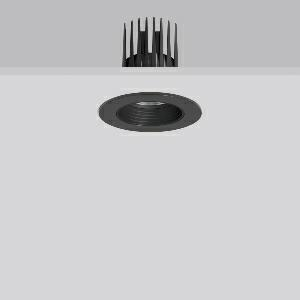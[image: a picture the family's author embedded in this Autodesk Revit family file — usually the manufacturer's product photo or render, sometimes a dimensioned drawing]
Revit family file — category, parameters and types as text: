
# Revit family: heledon_mini_e_901743_003_2_76_d9f7
name_source: partatom
category: Lighting Fixtures
units: mm (PartAtom-declared; Revit-internal decimal feet)

## family parameters
Cut with Voids When Loaded = No
Host = Face
Light Source = No
Part Type = Normal
Room Calculation Point = No
Round Connector Dimension = Use Diameter
Shared = No

## types (1)
- HELEDON mini E (1 x LED Modul 927, 2100 lm, 2700)
    Apparent Load = 20 VA
    Approval mark = CE
    CIE Flux Codes = 99 100 100 100 100
    Color Rendering = 92
    Color Temperature = 2700
    Default Elevation = 1800 mm
    Description = Series: HELEDON mini
Round recessed downlight. Housing: die-cast aluminium, powder-coated. Black plastic ring and recessed LED to prevent glare from the side. Optical assembly with lens made of plastic (polycarbonate) for the best homogeneous light distribution - can be changed without tools. Best colour rendering index Ra>90. Suitable for Recessed ceiling mounting. Installation without tools thanks to spring fastening system. Including separate LED converter with connecting cable 600 mm.High quality converter without flickering and stroboscopic effect. Through-wiring box (5 pole) available as accessory. The following accessories can be mounted without use of tools: interchangeable lenses, decorative glasses, honeycomb louvre, clear and frosted diffusers, white interchangeable plastic ring. 
Colour: deep black, matt (RAL 9005)
Diameter: 124 mm
Height: 3 mm
Cut-out diameter: 114 mm
Recess height: 170 mm
Luminaire: recess height: 120 mm
Lamp: LED
Socket: without socket
Colour temperature: 2700K
Colour rendering index (CRI): 92
System power: 20 W
Rated luminous flux: 2100 lm
Luminous efficiency: 105 lm/W
Control gear: Converter, dimmable, DALI
Protection class: II
Type of protection: IP 20
    Height = 0 mm  [stored 0 ft]
    Lamp = 1 x LED Modul 927
    Lamp Light Flux = 2100 lm
    Lamp count = 1
    Length = 124 mm  [stored 0.406824 ft]
    Lifetime = 50000 h
    Luminous efficacy = 105 lm/W
    Manufacturer = RZB
    ModVariant = No
    Model = 901743.003.2.76
    Mounting Place = Ceiling
    Mounting Type = Recessed
    Number of Poles = 1
    OnlyDefault = Yes
    Power Factor = 1
    Product Name = HELEDON mini E
    Product group = Recessed downlights
    ProductGroupID = 402
    Protection Class = Protection class II
    Protection Degree = IP 20
    RLX_Detail_Level = 1
    RLX_Emergency_Light_Flux = 0 lm
    RLX_Emergency_Type = 0
    RLX_Emergency_Type_DB = No
    RlxData = <blob elided: 125209 chars, md5=b85ec6eb>
    Socket = socket
    Standby Power = 0 W
    System Light Flux = 2100 lm
    System Power = 20 W
    Type Comments = Product without accessories
    Type Image = 901656.003.jpg
    URL = http://relux.com
    VarID = ---
    Voltage = 230 V
    Voltage Range = 220-240 V
    Weight = 0.00 kg
    Width = 0 mm  [stored 0 ft]

note: [stored X ft] marks values corroborated as IEEE doubles in the binary element streams (Revit-internal decimal feet)

## geometry (parser evidence)
native form markers: Blend x4, Sweep x10
no freeform markers — native parametric forms only
